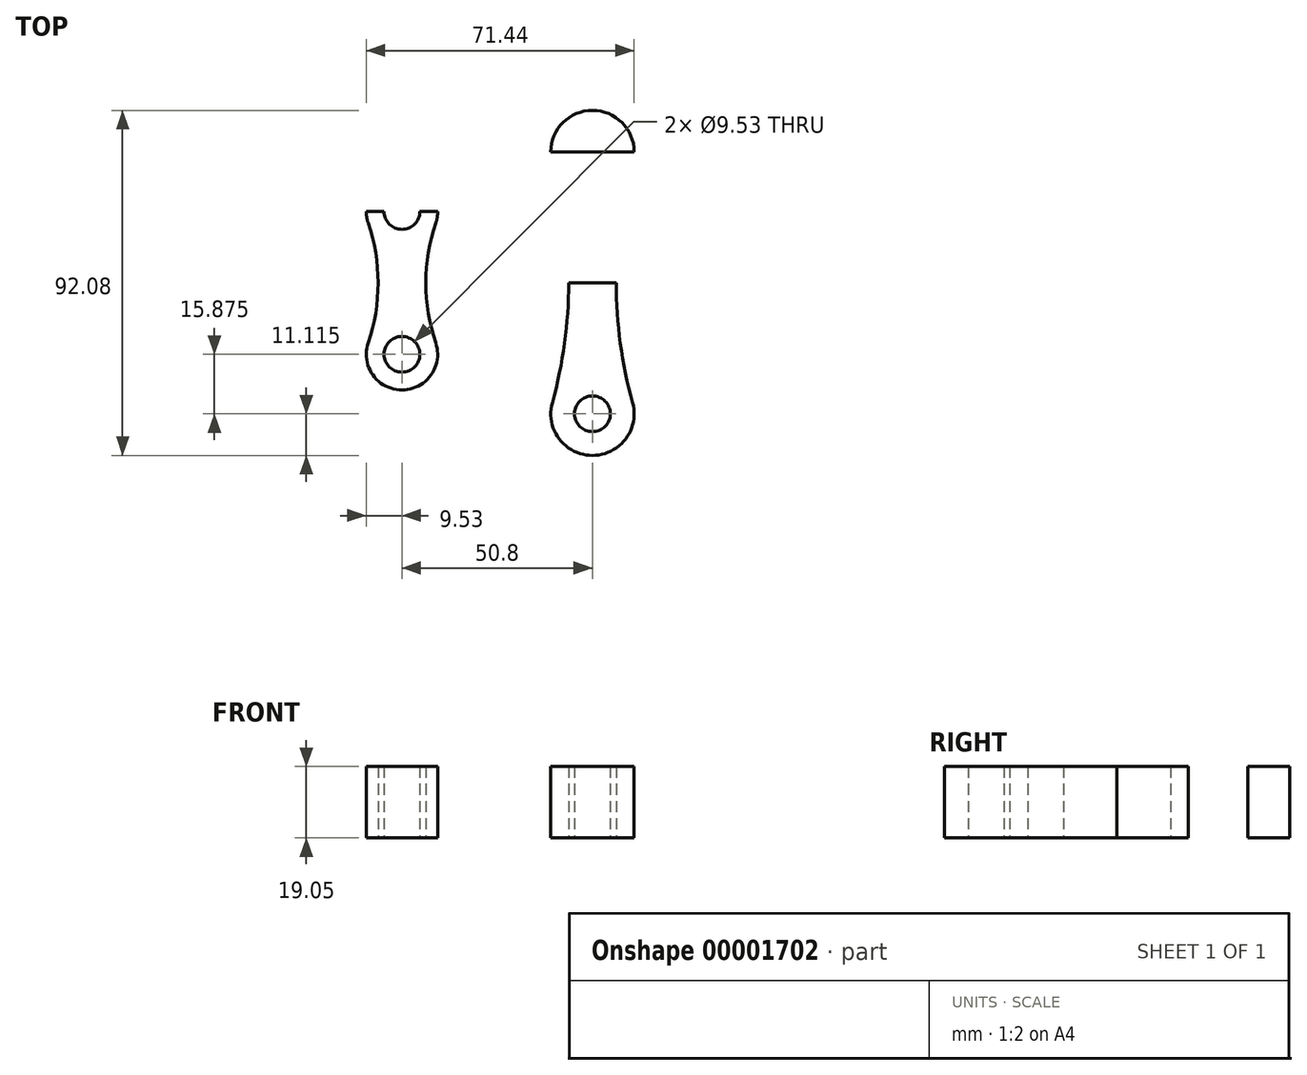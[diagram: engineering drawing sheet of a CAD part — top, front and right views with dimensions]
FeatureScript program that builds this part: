
annotation { "Feature Type Name" : "Feature", "Feature Type Description" : "" }
export const myFeature = defineFeature(function(context is Context, id is Id, definition is map)
    precondition{}
    {
        {
            var Q0;
            Q0=qCreatedBy(makeId("Top.planeOp"),FACE);
            var sketch = newSketch(context, id + "F0", { "sketchPlane" : qUnion([Q0])});
            skLineSegment(sketch, "E0", {"start": v(0, 19.05) * mm, "end": v(0, -19.05) * mm, "construction": true});
            skCircle(sketch, "E1", {"center": v(0, 19.05) * mm, "radius": 4.76 * mm});
            skCircle(sketch, "E2", {"center": v(0, -19.05) * mm, "radius": 4.76 * mm});
            skArc(sketch, "E3.0", {"start": v(9.01, 15.96) * mm, "mid": v(0, 28.58) * mm, "end": v(-9.01, 15.96) * mm});
            skArc(sketch, "E4.0", {"start": v(-9.01, -15.96) * mm, "mid": v(0, -28.58) * mm, "end": v(9.01, -15.96) * mm});
            skArc(sketch, "E5", {"start": v(-9.01, -15.96) * mm, "mid": v(-6.35, 0) * mm, "end": v(-9.01, 15.96) * mm});
            skArc(sketch, "E6.0.MirrorCS", {"start": v(9.01, -15.96) * mm, "mid": v(6.35, 0) * mm, "end": v(9.01, 15.96) * mm});
            skLineSegment(sketch, "E7", {"start": v(-9.53, 19.05) * mm, "end": v(9.52, 19.05) * mm});
            skLineSegment(sketch, "E8", {"start": v(0, 28.58) * mm, "end": v(0, -28.58) * mm});
            skLineSegment(sketch, "E9", {"start": v(-9.52, -19.05) * mm, "end": v(9.53, -19.05) * mm});
            skLineSegment(sketch, "E10", {"start": v(0, 0) * mm, "end": v(-6.35, 0) * mm});
            skLineSegment(sketch, "E11", {"start": v(0, 0) * mm, "end": v(6.35, 0) * mm});
            skSolve(sketch);
        }
        {
            var Q0;
            Q0=qCreatedBy(makeId("Top.planeOp"),FACE);
            var sketch = newSketch(context, id + "F1", { "sketchPlane" : qUnion([Q0])});
            skLineSegment(sketch, "E12", {"start": v(50.8, 46.04) * mm, "end": v(50.8, -46.04) * mm});
            skCircle(sketch, "E13", {"center": v(50.8, 34.93) * mm, "radius": 4.76 * mm});
            skCircle(sketch, "E14", {"center": v(50.8, -34.92) * mm, "radius": 4.76 * mm});
            skLineSegment(sketch, "E15", {"start": v(50.8, 0) * mm, "end": v(0, 0) * mm, "construction": true});
            skArc(sketch, "E16.0", {"start": v(61.5, 31.95) * mm, "mid": v(50.8, 46.04) * mm, "end": v(40.1, 31.95) * mm});
            skArc(sketch, "E17.0", {"start": v(40.1, -31.95) * mm, "mid": v(50.8, -46.04) * mm, "end": v(61.5, -31.95) * mm});
            skArc(sketch, "E18", {"start": v(40.1, -31.95) * mm, "mid": v(44.45, 0) * mm, "end": v(40.1, 31.95) * mm});
            skArc(sketch, "E19", {"start": v(61.5, 31.95) * mm, "mid": v(57.15, 0) * mm, "end": v(61.5, -31.95) * mm});
            skLineSegment(sketch, "E20", {"start": v(39.69, 34.93) * mm, "end": v(61.91, 34.93) * mm});
            skLineSegment(sketch, "E21", {"start": v(44.45, 0) * mm, "end": v(57.15, 0) * mm});
            skLineSegment(sketch, "E22", {"start": v(39.69, -34.92) * mm, "end": v(61.91, -34.92) * mm});
            skSolve(sketch);
        }
        {
            var Q0;
            {var subQ0=sQuery(id+"F1.wireOp",EDGE,"E21");var subQ1=sQuery(id+"F1.wireOp",EDGE,"E12");var subQ2=makeQuery(id+"F1.imprint","INTERSECT",VERTEX,{"derivedFrom":[subQ1,subQ0]});Q0=makeQuery(id+"F1.imprint","IMPRINT",FACE,{"disambiguationData":[TD([[makeQuery(id+"F1.imprint","IMPRINT",EDGE,{"disambiguationData":[TD([[subQ2,-1.0]])],"derivedFrom":subQ1}),-1.0]])]});}
            var Q1;
            {var subQ3=sQuery(id+"F1.wireOp",EDGE,"E17.0");var subQ5=sQuery(id+"F1.wireOp",EDGE,"E12");var subQ6=makeQuery(id+"F1.imprint","INTERSECT",VERTEX,{"derivedFrom":[subQ5,subQ3]});Q1=makeQuery(id+"F1.imprint","IMPRINT",FACE,{"disambiguationData":[TD([[makeQuery(id+"F1.imprint","IMPRINT",EDGE,{"disambiguationData":[TD([[subQ6,1.0]])],"derivedFrom":subQ5}),-1.0]])]});}
            var Q2;
            {var subQ3=sQuery(id+"F1.wireOp",EDGE,"E17.0");var subQ5=sQuery(id+"F1.wireOp",EDGE,"E12");var subQ6=makeQuery(id+"F1.imprint","INTERSECT",VERTEX,{"derivedFrom":[subQ5,subQ3]});Q2=makeQuery(id+"F1.imprint","IMPRINT",FACE,{"disambiguationData":[TD([[makeQuery(id+"F1.imprint","IMPRINT",EDGE,{"disambiguationData":[TD([[subQ6,1.0]])],"derivedFrom":subQ5}),1.0]])]});}
            var Q3;
            {var subQ5=sQuery(id+"F1.wireOp",EDGE,"E21");var subQ6=sQuery(id+"F1.wireOp",EDGE,"E12");var subQ7=makeQuery(id+"F1.imprint","INTERSECT",VERTEX,{"derivedFrom":[subQ6,subQ5]});Q3=makeQuery(id+"F1.imprint","IMPRINT",FACE,{"disambiguationData":[TD([[makeQuery(id+"F1.imprint","IMPRINT",EDGE,{"disambiguationData":[TD([[subQ7,-1.0]])],"derivedFrom":subQ6}),1.0]])]});}
            var Q4;
            {var subQ1=sQuery(id+"F1.wireOp",EDGE,"E12");var subQ6=sQuery(id+"F1.wireOp",EDGE,"E13");var subQ11=makeQuery(id+"F1.imprint","INTERSECT",VERTEX,{"disambiguationData":[OD(1.0)],"derivedFrom":[subQ1,subQ6]});Q4=makeQuery(id+"F1.imprint","IMPRINT",FACE,{"disambiguationData":[TD([[makeQuery(id+"F1.imprint","IMPRINT",EDGE,{"disambiguationData":[TD([[subQ11,-1.0]])],"derivedFrom":subQ1}),1.0]])]});}
            var Q5;
            {var subQ3=sQuery(id+"F1.wireOp",EDGE,"E16.0");var subQ5=sQuery(id+"F1.wireOp",EDGE,"E12");var subQ6=makeQuery(id+"F1.imprint","INTERSECT",VERTEX,{"derivedFrom":[subQ5,subQ3]});Q5=makeQuery(id+"F1.imprint","IMPRINT",FACE,{"disambiguationData":[TD([[makeQuery(id+"F1.imprint","IMPRINT",EDGE,{"disambiguationData":[TD([[subQ6,-1.0]])],"derivedFrom":subQ5}),1.0]])]});}
            var Q6;
            {var subQ3=sQuery(id+"F1.wireOp",EDGE,"E16.0");var subQ5=sQuery(id+"F1.wireOp",EDGE,"E12");var subQ6=makeQuery(id+"F1.imprint","INTERSECT",VERTEX,{"derivedFrom":[subQ5,subQ3]});Q6=makeQuery(id+"F1.imprint","IMPRINT",FACE,{"disambiguationData":[TD([[makeQuery(id+"F1.imprint","IMPRINT",EDGE,{"disambiguationData":[TD([[subQ6,-1.0]])],"derivedFrom":subQ5}),-1.0]])]});}
            var Q7;
            {var subQ1=sQuery(id+"F1.wireOp",EDGE,"E12");var subQ6=sQuery(id+"F1.wireOp",EDGE,"E13");var subQ11=makeQuery(id+"F1.imprint","INTERSECT",VERTEX,{"disambiguationData":[OD(1.0)],"derivedFrom":[subQ1,subQ6]});Q7=makeQuery(id+"F1.imprint","IMPRINT",FACE,{"disambiguationData":[TD([[makeQuery(id+"F1.imprint","IMPRINT",EDGE,{"disambiguationData":[TD([[subQ11,-1.0]])],"derivedFrom":subQ1}),-1.0]])]});}
            extrude(context, id + "F2", {"entities" : qUnion([Q0, Q1, Q2, Q3, Q4, Q5, Q6, Q7]), "depth" : 19.05 * mm});
        }
        {
            var Q0;
            {var subQ0=sQuery(id+"F0.wireOp",EDGE,"E11");Q0=makeQuery(id+"F0.imprint","IMPRINT",FACE,{"disambiguationData":[TD([[makeQuery(id+"F0.imprint","IMPRINT",EDGE,{"derivedFrom":subQ0}),1.0]])]});}
            var Q1;
            {var subQ0=sQuery(id+"F0.wireOp",EDGE,"E8");var subQ1=sQuery(id+"F0.wireOp",EDGE,"E1");var subQ2=makeQuery(id+"F0.imprint","INTERSECT",VERTEX,{"disambiguationData":[OD(0.0)],"derivedFrom":[subQ1,subQ0]});Q1=makeQuery(id+"F0.imprint","IMPRINT",FACE,{"disambiguationData":[TD([[makeQuery(id+"F0.imprint","IMPRINT",EDGE,{"disambiguationData":[TD([[subQ2,1.0]])],"derivedFrom":subQ1}),-1.0]])]});}
            var Q2;
            {var subQ0=sQuery(id+"F0.wireOp",EDGE,"E8");var subQ1=sQuery(id+"F0.wireOp",EDGE,"E1");var subQ2=makeQuery(id+"F0.imprint","INTERSECT",VERTEX,{"disambiguationData":[OD(0.0)],"derivedFrom":[subQ1,subQ0]});Q2=makeQuery(id+"F0.imprint","IMPRINT",FACE,{"disambiguationData":[TD([[makeQuery(id+"F0.imprint","IMPRINT",EDGE,{"disambiguationData":[TD([[subQ2,-1.0]])],"derivedFrom":subQ1}),-1.0]])]});}
            var Q3;
            {var subQ0=sQuery(id+"F0.wireOp",EDGE,"E10");Q3=makeQuery(id+"F0.imprint","IMPRINT",FACE,{"disambiguationData":[TD([[makeQuery(id+"F0.imprint","IMPRINT",EDGE,{"derivedFrom":subQ0}),-1.0]])]});}
            var Q4;
            {var subQ0=sQuery(id+"F0.wireOp",EDGE,"E10");Q4=makeQuery(id+"F0.imprint","IMPRINT",FACE,{"disambiguationData":[TD([[makeQuery(id+"F0.imprint","IMPRINT",EDGE,{"derivedFrom":subQ0}),1.0]])]});}
            var Q5;
            {var subQ0=sQuery(id+"F0.wireOp",EDGE,"E11");Q5=makeQuery(id+"F0.imprint","IMPRINT",FACE,{"disambiguationData":[TD([[makeQuery(id+"F0.imprint","IMPRINT",EDGE,{"derivedFrom":subQ0}),-1.0]])]});}
            var Q6;
            {var subQ0=sQuery(id+"F0.wireOp",EDGE,"E9");var subQ1=sQuery(id+"F0.wireOp",EDGE,"E2");var subQ2=makeQuery(id+"F0.imprint","INTERSECT",VERTEX,{"disambiguationData":[OD(0.0)],"derivedFrom":[subQ1,subQ0]});Q6=makeQuery(id+"F0.imprint","IMPRINT",FACE,{"disambiguationData":[TD([[makeQuery(id+"F0.imprint","IMPRINT",EDGE,{"disambiguationData":[TD([[subQ2,1.0]])],"derivedFrom":subQ1}),-1.0]])]});}
            var Q7;
            {var subQ0=sQuery(id+"F0.wireOp",EDGE,"E9");var subQ1=sQuery(id+"F0.wireOp",EDGE,"E2");var subQ2=makeQuery(id+"F0.imprint","INTERSECT",VERTEX,{"disambiguationData":[OD(1.0)],"derivedFrom":[subQ1,subQ0]});Q7=makeQuery(id+"F0.imprint","IMPRINT",FACE,{"disambiguationData":[TD([[makeQuery(id+"F0.imprint","IMPRINT",EDGE,{"disambiguationData":[TD([[subQ2,-1.0]])],"derivedFrom":subQ1}),-1.0]])]});}
            extrude(context, id + "F3", {"entities" : qUnion([Q0, Q1, Q2, Q3, Q4, Q5, Q6, Q7]), "depth" : 19.05 * mm});
        }
    });
